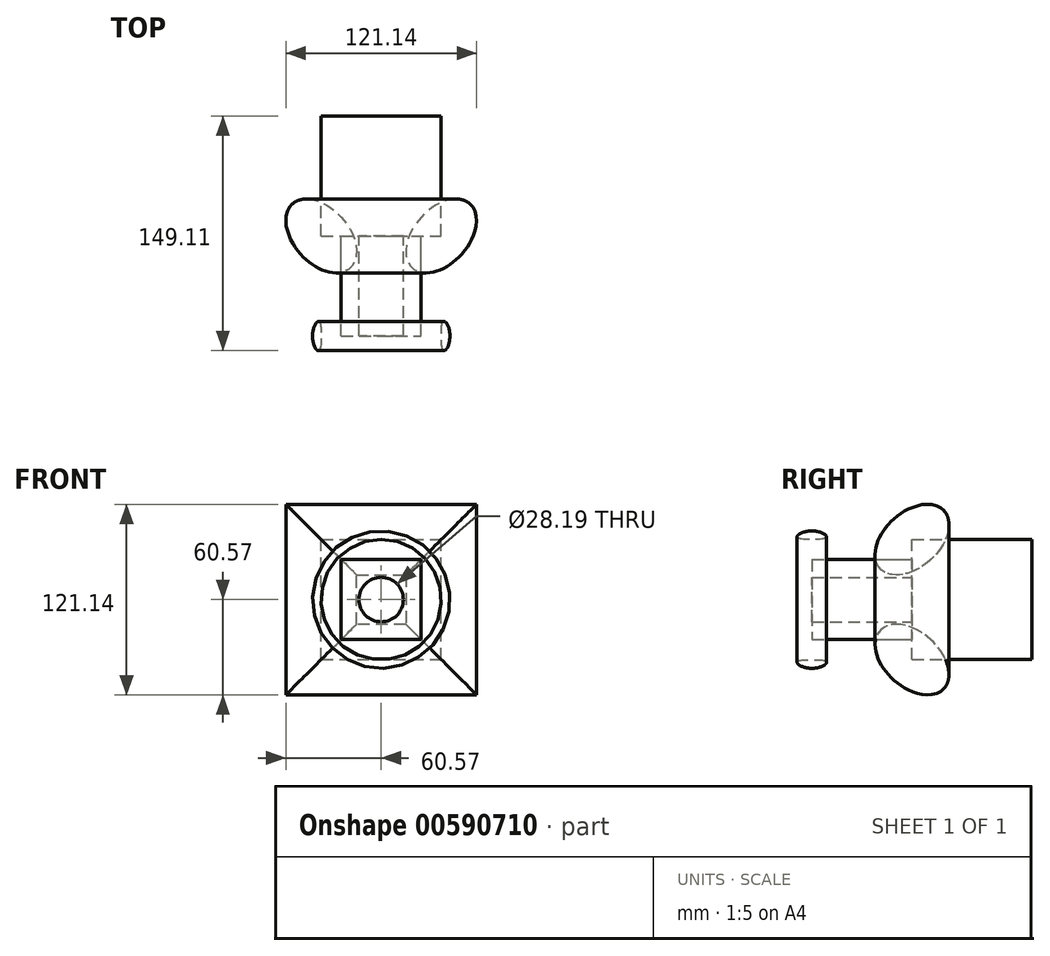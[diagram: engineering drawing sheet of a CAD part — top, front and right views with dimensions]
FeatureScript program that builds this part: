
annotation { "Feature Type Name" : "Feature", "Feature Type Description" : "" }
export const myFeature = defineFeature(function(context is Context, id is Id, definition is map)
    precondition{}
    {
        {
            var Q0;
            Q0=qCreatedBy(makeId("Front.planeOp"),FACE);
            var sketch = newSketch(context, id + "F0", { "sketchPlane" : qUnion([Q0])});
            skLineSegment(sketch, "E0.bottom", {"start": v(0, 0) * mm, "end": v(76.2, 0) * mm});
            skLineSegment(sketch, "E0.top", {"start": v(0, 76.2) * mm, "end": v(76.2, 76.2) * mm});
            skLineSegment(sketch, "E0.left", {"start": v(0, 0) * mm, "end": v(0, 76.2) * mm});
            skLineSegment(sketch, "E0.right", {"start": v(76.2, 0) * mm, "end": v(76.2, 76.2) * mm});
            skSolve(sketch);
        }
        {
            var Q0;
            Q0=makeQuery(id+"F0.imprint","IMPRINT",FACE,{"disambiguationData":[TD([[makeQuery(id+"F0.imprint","IMPRINT",EDGE,{"derivedFrom":sQuery(id+"F0.wireOp",EDGE,"E0.bottom")}),1.0]])]});
            extrude(context, id + "F1", {"entities" : qUnion([Q0]), "depth" : 76.2 * mm, "offsetDistance" : 25.4 * mm});
        }
        {
            var Q0;
            Q0=makeQuery(id+"F1.opExtrude","SWEPT_FACE",FACE,{"disambiguationData":[OSD([sQuery(id+"F0.wireOp",EDGE,"E0.top")])]});
            var sketch = newSketch(context, id + "F2", { "sketchPlane" : qUnion([Q0])});
            skEllipse(sketch, "E1", {"center": v(76.2, -76.2) * mm, "majorRadius": 17.42 * mm, "minorRadius": 27.4 * mm, "majorAxis": v(0.74, -0.67)});
            skSolve(sketch);
        }
        {
            var Q0;
            {var subQ0=sQuery(id+"F2.wireOp",EDGE,"E1");var subQ1=sQuery(id+"F0.wireOp",EDGE,"E0.top");var subQ4=makeQuery(id+"F1.opExtrude","CAP_EDGE",EDGE,{"disambiguationData":[OSD([subQ1])],"isStart":false});var subQ5=makeQuery(id+"F2.imprint","INTERSECT",VERTEX,{"derivedFrom":[subQ4,subQ0]});Q0=makeQuery(id+"F2.imprint","IMPRINT",FACE,{"disambiguationData":[TD([[makeQuery(id+"F2.imprint","IMPRINT",EDGE,{"disambiguationData":[TD([[subQ5,-1.0]])],"derivedFrom":subQ0}),1.0]])]});}
            var Q1;
            {var subQ0=sQuery(id+"F2.wireOp",EDGE,"E1");var subQ1=sQuery(id+"F0.wireOp",EDGE,"E0.top");var subQ4=makeQuery(id+"F1.opExtrude","CAP_EDGE",EDGE,{"disambiguationData":[OSD([subQ1])],"isStart":false});var subQ5=makeQuery(id+"F2.imprint","INTERSECT",VERTEX,{"derivedFrom":[subQ4,subQ0]});Q1=makeQuery(id+"F2.imprint","IMPRINT",FACE,{"disambiguationData":[TD([[makeQuery(id+"F2.imprint","IMPRINT",EDGE,{"disambiguationData":[TD([[subQ5,1.0]])],"derivedFrom":subQ0}),1.0]])]});}
            var Q2;
            Q2=makeQuery(id+"F1.opExtrude","CAP_EDGE",EDGE,{"disambiguationData":[OSD([sQuery(id+"F0.wireOp",EDGE,"E0.right")])],"isStart":false});
            var Q3;
            Q3=makeQuery(id+"F1.opExtrude","CAP_EDGE",EDGE,{"disambiguationData":[OSD([sQuery(id+"F0.wireOp",EDGE,"E0.top")])],"isStart":false});
            var Q4;
            Q4=makeQuery(id+"F1.opExtrude","CAP_EDGE",EDGE,{"disambiguationData":[OSD([sQuery(id+"F0.wireOp",EDGE,"E0.left")])],"isStart":false});
            var Q5;
            Q5=makeQuery(id+"F1.opExtrude","CAP_EDGE",EDGE,{"disambiguationData":[OSD([sQuery(id+"F0.wireOp",EDGE,"E0.bottom")])],"isStart":false});
            sweep(context, id + "F3", {"profiles" : qUnion([Q0, Q1]), "path" : qUnion([Q2, Q3, Q4, Q5])});
        }
        {
            var Q0;
            Q0=makeQuery(id+"F1.opExtrude","CAP_FACE",FACE,{"disambiguationData":[OSD([sQuery(id+"F0.wireOp",EDGE,"E0.bottom"),sQuery(id+"F0.wireOp",EDGE,"E0.top"),sQuery(id+"F0.wireOp",EDGE,"E0.left"),sQuery(id+"F0.wireOp",EDGE,"E0.right")])],"isStart":false});
            var sketch = newSketch(context, id + "F4", { "sketchPlane" : qUnion([Q0])});
            skLineSegment(sketch, "E2", {"start": v(38.1, 76.2) * mm, "end": v(38.1, 0) * mm, "construction": true});
            skCircle(sketch, "E3", {"center": v(38.1, 38.1) * mm, "radius": 14.1 * mm});
            skLineSegment(sketch, "E4.bottom", {"start": v(12.7, 63.5) * mm, "end": v(63.5, 63.5) * mm});
            skLineSegment(sketch, "E4.top", {"start": v(12.7, 12.7) * mm, "end": v(63.5, 12.7) * mm});
            skLineSegment(sketch, "E4.left", {"start": v(12.7, 63.5) * mm, "end": v(12.7, 12.7) * mm});
            skLineSegment(sketch, "E4.right", {"start": v(63.5, 63.5) * mm, "end": v(63.5, 12.7) * mm});
            skSolve(sketch);
        }
        {
            var Q0;
            Q0=makeQuery(id+"F4.imprint","IMPRINT",FACE,{"disambiguationData":[TD([[makeQuery(id+"F4.imprint","IMPRINT",EDGE,{"derivedFrom":sQuery(id+"F4.wireOp",EDGE,"E3")}),-1.0]])]});
            extrude(context, id + "F5", {"entities" : qUnion([Q0]), "depth" : 63.5 * mm, "offsetDistance" : 25.4 * mm});
        }
        {
            var Q0;
            Q0=qCreatedBy(makeId("Right.planeOp"),FACE);
            var sketch = newSketch(context, id + "F6", { "sketchPlane" : qUnion([Q0])});
            skCircle(sketch, "E5", {"center": v(-139.8, 26.14) * mm, "radius": 9.3 * mm});
            skSolve(sketch);
        }
        {
            var Q0;
            Q0=makeQuery(id+"F6.imprint","IMPRINT",FACE,{"disambiguationData":[TD([[makeQuery(id+"F6.imprint","IMPRINT",EDGE,{"derivedFrom":sQuery(id+"F6.wireOp",EDGE,"E5")}),1.0]])]});
            var Q1;
            Q1=makeQuery(id+"F5.opExtrude","CAP_EDGE",EDGE,{"disambiguationData":[OSD([sQuery(id+"F4.wireOp",EDGE,"E3")])],"isStart":false});
            revolve(context, id + "F7", {"entities" : qUnion([Q0]), "axis" : qUnion([Q1]), "revolveType" : RevolveType.FULL});
        }
    });
